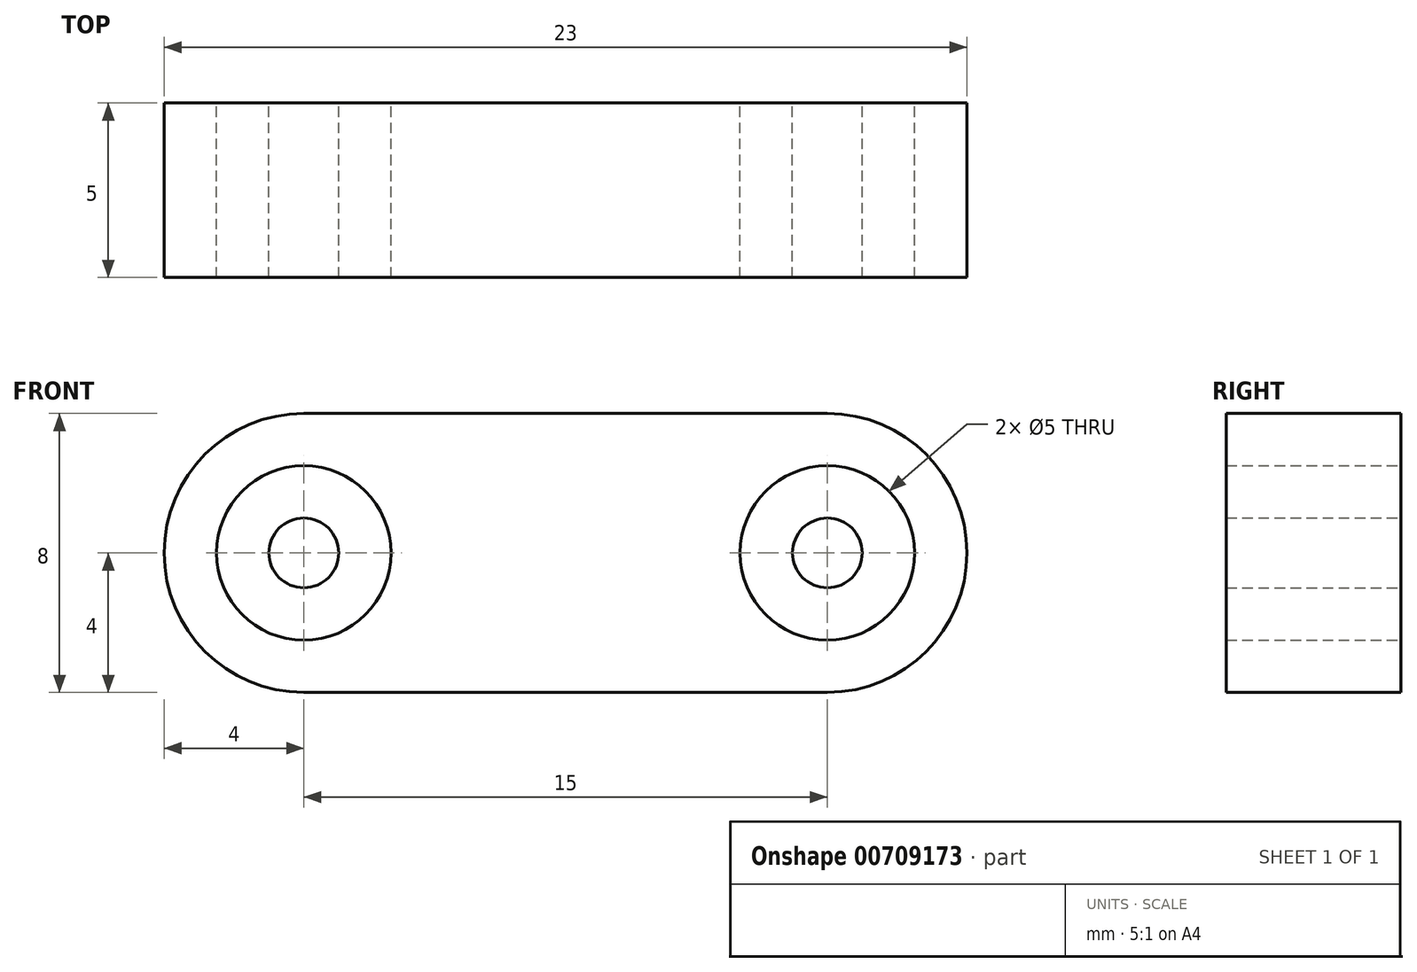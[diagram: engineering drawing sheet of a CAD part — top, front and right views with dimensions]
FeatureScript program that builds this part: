
annotation { "Feature Type Name" : "Feature", "Feature Type Description" : "" }
export const myFeature = defineFeature(function(context is Context, id is Id, definition is map)
    precondition{}
    {
        {
            var Q0;
            Q0=qCreatedBy(makeId("Front.planeOp"),FACE);
            var sketch = newSketch(context, id + "F0", { "sketchPlane" : qUnion([Q0])});
            skArc(sketch, "E0", {"start": v(0, 4) * mm, "mid": v(-4, 0) * mm, "end": v(0, -4) * mm});
            skArc(sketch, "E1", {"start": v(15, -4) * mm, "mid": v(19, 0) * mm, "end": v(15, 4) * mm});
            skLineSegment(sketch, "E2", {"start": v(0, 4) * mm, "end": v(15, 4) * mm});
            skLineSegment(sketch, "E3", {"start": v(0, -4) * mm, "end": v(15, -4) * mm});
            skCircle(sketch, "E4", {"center": v(0, 0) * mm, "radius": 2.5 * mm});
            skCircle(sketch, "E5", {"center": v(15, 0) * mm, "radius": 2.5 * mm});
            skCircle(sketch, "E6", {"center": v(15, 0) * mm, "radius": 1 * mm});
            skCircle(sketch, "E7", {"center": v(0, 0) * mm, "radius": 1 * mm});
            skSolve(sketch);
        }
        {
            var Q0;
            Q0=makeQuery(id+"F0.imprint","IMPRINT",FACE,{"disambiguationData":[TD([[makeQuery(id+"F0.imprint","IMPRINT",EDGE,{"derivedFrom":sQuery(id+"F0.wireOp",EDGE,"E0")}),1.0]])]});
            var Q1;
            Q1=makeQuery(id+"F0.imprint","IMPRINT",FACE,{"disambiguationData":[TD([[makeQuery(id+"F0.imprint","IMPRINT",EDGE,{"derivedFrom":sQuery(id+"F0.wireOp",EDGE,"E7")}),1.0]])]});
            var Q2;
            Q2=makeQuery(id+"F0.imprint","IMPRINT",FACE,{"disambiguationData":[TD([[makeQuery(id+"F0.imprint","IMPRINT",EDGE,{"derivedFrom":sQuery(id+"F0.wireOp",EDGE,"E6")}),1.0]])]});
            extrude(context, id + "F1", {"entities" : qUnion([Q0, Q1, Q2]), "depth" : 5 * mm, "offsetDistance" : 25 * mm});
        }
    });
